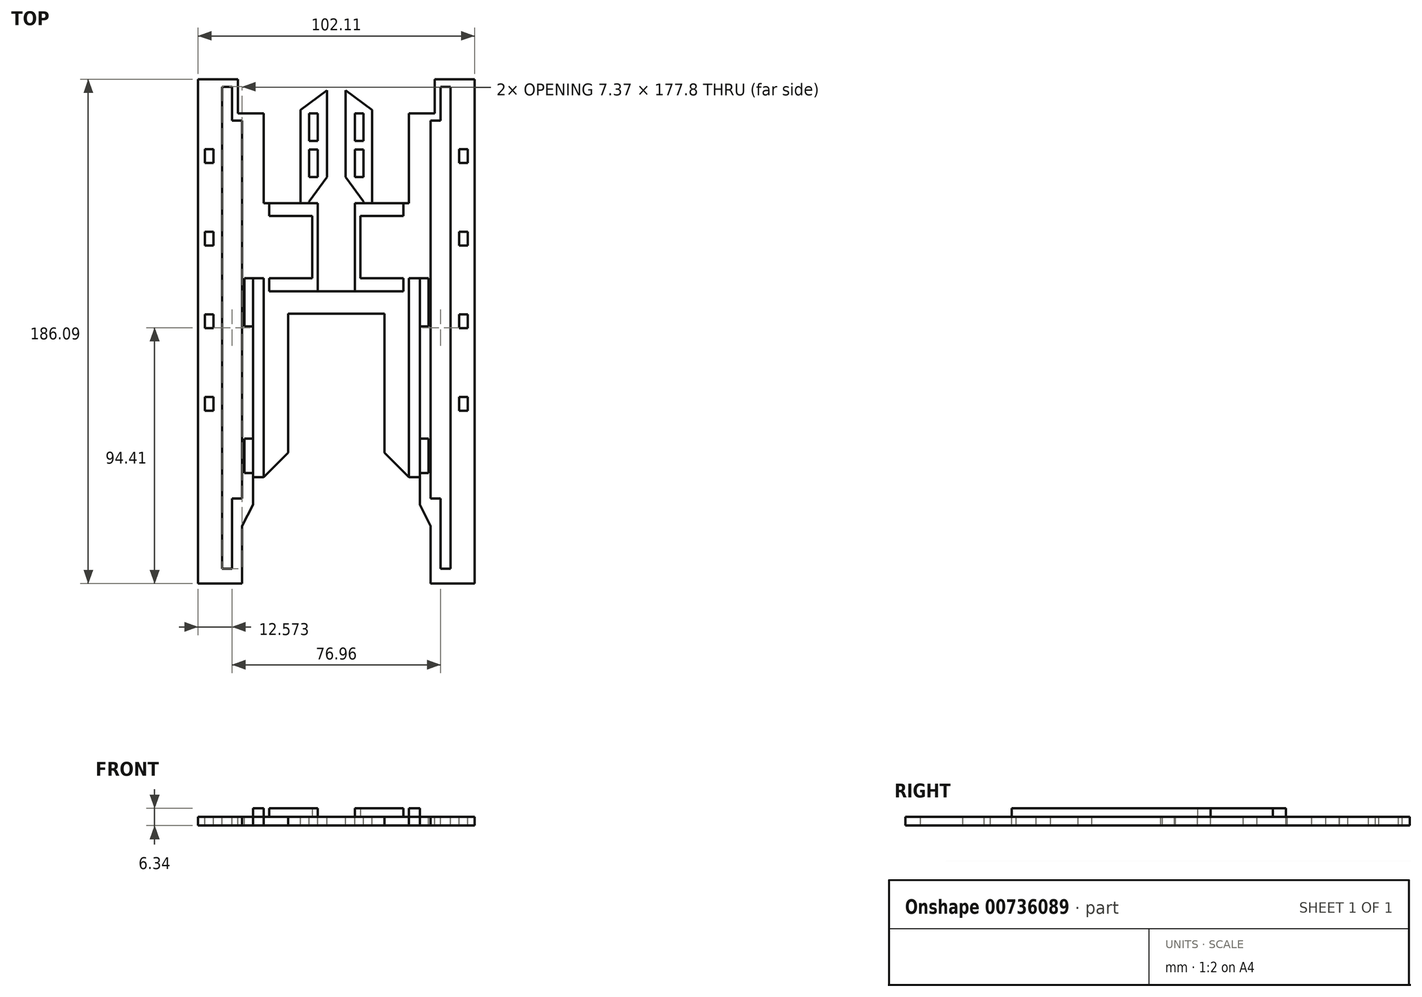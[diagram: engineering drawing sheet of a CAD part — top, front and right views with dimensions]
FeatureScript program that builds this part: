
annotation { "Feature Type Name" : "Feature", "Feature Type Description" : "" }
export const myFeature = defineFeature(function(context is Context, id is Id, definition is map)
    precondition{}
    {
        {
            var Q0;
            Q0=qCreatedBy(makeId("Top.planeOp"),FACE);
            var sketch = newSketch(context, id + "F0", { "sketchPlane" : qUnion([Q0])});
            skLineSegment(sketch, "E0.bottom", {"start": v(-53.6, 68.58) * mm, "end": v(0, 68.58) * mm});
            skLineSegment(sketch, "E0.top", {"start": v(-53.6, 0) * mm, "end": v(0, 0) * mm});
            skLineSegment(sketch, "E0.left", {"start": v(-53.6, 68.58) * mm, "end": v(-53.6, 0) * mm});
            skLineSegment(sketch, "E0.right", {"start": v(0, 68.58) * mm, "end": v(0, 0) * mm});
            skLineSegment(sketch, "E1", {"start": v(-53.6, 0) * mm, "end": v(-44.61, 8.98) * mm});
            skLineSegment(sketch, "E2", {"start": v(-44.61, 8.98) * mm, "end": v(-44.61, 68.58) * mm});
            skLineSegment(sketch, "E3", {"start": v(-53.6, 68.58) * mm, "end": v(-53.6, 73.33) * mm});
            skLineSegment(sketch, "E4", {"start": v(-53.6, 73.33) * mm, "end": v(-57.6, 73.33) * mm});
            skLineSegment(sketch, "E5", {"start": v(-57.6, 73.33) * mm, "end": v(-57.6, 0) * mm});
            skLineSegment(sketch, "E6", {"start": v(-57.6, 0) * mm, "end": v(-53.6, 0) * mm});
            skLineSegment(sketch, "E7", {"start": v(-53.6, 68.58) * mm, "end": v(-51.6, 68.58) * mm});
            skLineSegment(sketch, "E8", {"start": v(-53.6, 73.33) * mm, "end": v(-35.64, 73.33) * mm});
            skLineSegment(sketch, "E9", {"start": v(-35.64, 73.33) * mm, "end": v(-35.64, 96.37) * mm});
            skLineSegment(sketch, "E10", {"start": v(-51.6, 68.58) * mm, "end": v(-51.6, 73.33) * mm});
            skLineSegment(sketch, "E11", {"start": v(-26.8, 0) * mm, "end": v(-26.8, 68.58) * mm});
            skLineSegment(sketch, "E12", {"start": v(-33.62, 90.8) * mm, "end": v(-33.62, 68.58) * mm});
            skLineSegment(sketch, "E13", {"start": v(-35.64, 96.37) * mm, "end": v(-51.59, 96.37) * mm});
            skLineSegment(sketch, "E14", {"start": v(-53.6, 73.33) * mm, "end": v(-53.6, 96.37) * mm});
            skLineSegment(sketch, "E15", {"start": v(-53.6, 96.37) * mm, "end": v(-51.59, 96.37) * mm});
            skLineSegment(sketch, "E16", {"start": v(-53.6, 96.37) * mm, "end": v(-53.6, 101.12) * mm});
            skLineSegment(sketch, "E17", {"start": v(-53.6, 101.12) * mm, "end": v(-33.62, 101.12) * mm});
            skLineSegment(sketch, "E18", {"start": v(-33.62, 101.12) * mm, "end": v(-33.62, 90.8) * mm});
            skLineSegment(sketch, "E19", {"start": v(-51.59, 96.37) * mm, "end": v(-51.59, 101.12) * mm});
            skLineSegment(sketch, "E20", {"start": v(-57.6, 73.33) * mm, "end": v(-57.6, 55.55) * mm});
            skLineSegment(sketch, "E21", {"start": v(-57.6, 55.55) * mm, "end": v(-60.77, 55.55) * mm});
            skLineSegment(sketch, "E22", {"start": v(-60.77, 55.55) * mm, "end": v(-60.77, 73.33) * mm});
            skLineSegment(sketch, "E23", {"start": v(-60.77, 73.33) * mm, "end": v(-57.6, 73.33) * mm});
            skLineSegment(sketch, "E24", {"start": v(-60.77, 73.33) * mm, "end": v(-61.6, 73.33) * mm});
            skLineSegment(sketch, "E25", {"start": v(-57.6, 0) * mm, "end": v(-57.6, 1.54) * mm});
            skPoint(sketch, "E25.endSnap0", {"position": v(-49.1, 4.5) * mm});
            skLineSegment(sketch, "E26", {"start": v(-57.6, 1.54) * mm, "end": v(-60.77, 1.54) * mm});
            skLineSegment(sketch, "E27", {"start": v(-60.77, 1.54) * mm, "end": v(-60.77, 14.24) * mm});
            skLineSegment(sketch, "E28", {"start": v(-60.77, 14.24) * mm, "end": v(-57.6, 14.24) * mm});
            skLineSegment(sketch, "E29", {"start": v(-61.6, 73.33) * mm, "end": v(-61.6, -7.9) * mm});
            skLineSegment(sketch, "E30", {"start": v(-61.6, -7.9) * mm, "end": v(-57.6, 0) * mm});
            skLineSegment(sketch, "E31", {"start": v(-61.6, -7.9) * mm, "end": v(-65.28, -7.9) * mm});
            skLineSegment(sketch, "E32", {"start": v(-65.28, -7.9) * mm, "end": v(-65.28, -33.74) * mm});
            skLineSegment(sketch, "E33", {"start": v(-65.28, -33.74) * mm, "end": v(-68.96, -33.74) * mm});
            skLineSegment(sketch, "E34", {"start": v(-68.96, -33.74) * mm, "end": v(-68.96, 144.06) * mm});
            skLineSegment(sketch, "E35", {"start": v(-68.96, 144.06) * mm, "end": v(-65.28, 144.06) * mm});
            skLineSegment(sketch, "E36", {"start": v(-65.28, 144.06) * mm, "end": v(-65.28, 131.61) * mm});
            skLineSegment(sketch, "E37", {"start": v(-65.28, 131.61) * mm, "end": v(-61.6, 131.61) * mm});
            skLineSegment(sketch, "E38", {"start": v(-61.6, 131.61) * mm, "end": v(-61.6, 73.33) * mm});
            skLineSegment(sketch, "E39", {"start": v(-53.6, 101.12) * mm, "end": v(-53.6, 134.17) * mm});
            skLineSegment(sketch, "E40", {"start": v(-77.85, 146.84) * mm, "end": v(-77.85, -39.25) * mm});
            skLineSegment(sketch, "E41", {"start": v(-77.85, -39.25) * mm, "end": v(-61.6, -39.25) * mm});
            skLineSegment(sketch, "E42", {"start": v(-61.6, -39.25) * mm, "end": v(-61.6, -18.06) * mm});
            skLineSegment(sketch, "E43", {"start": v(-61.6, -18.06) * mm, "end": v(-57.6, -10.16) * mm});
            skLineSegment(sketch, "E44", {"start": v(-57.6, -10.16) * mm, "end": v(-57.6, 0) * mm});
            skLineSegment(sketch, "E45", {"start": v(-65.28, -33.74) * mm, "end": v(-65.28, -39.25) * mm});
            skLineSegment(sketch, "E46", {"start": v(-65.28, -39.25) * mm, "end": v(-61.6, -39.25) * mm});
            skLineSegment(sketch, "E47", {"start": v(-44.61, 60.36) * mm, "end": v(-26.8, 60.36) * mm});
            skLineSegment(sketch, "E48", {"start": v(-36.8, 134.17) * mm, "end": v(-36.8, 124) * mm});
            skLineSegment(sketch, "E49", {"start": v(-36.8, 124) * mm, "end": v(-36.8, 120.83) * mm});
            skLineSegment(sketch, "E50", {"start": v(-36.8, 120.83) * mm, "end": v(-36.8, 110.67) * mm});
            skLineSegment(sketch, "E51", {"start": v(-36.8, 110.67) * mm, "end": v(-33.62, 110.67) * mm});
            skLineSegment(sketch, "E52", {"start": v(-33.62, 110.67) * mm, "end": v(-33.62, 134.17) * mm});
            skLineSegment(sketch, "E53", {"start": v(-33.62, 134.17) * mm, "end": v(-36.8, 134.17) * mm});
            skLineSegment(sketch, "E54", {"start": v(-33.62, 110.67) * mm, "end": v(-30.2, 110.67) * mm});
            skLineSegment(sketch, "E55", {"start": v(-30.2, 110.67) * mm, "end": v(-36.8, 101.66) * mm});
            skLineSegment(sketch, "E56", {"start": v(-30.2, 110.67) * mm, "end": v(-30.2, 142.73) * mm});
            skLineSegment(sketch, "E57", {"start": v(-33.62, 101.12) * mm, "end": v(-36.8, 101.12) * mm});
            skLineSegment(sketch, "E58", {"start": v(-36.8, 110.67) * mm, "end": v(-36.8, 101.12) * mm});
            skLineSegment(sketch, "E59", {"start": v(-36.8, 101.12) * mm, "end": v(-39.97, 101.12) * mm});
            skLineSegment(sketch, "E60", {"start": v(-39.97, 101.12) * mm, "end": v(-39.97, 135.48) * mm});
            skLineSegment(sketch, "E61", {"start": v(-30.2, 142.73) * mm, "end": v(-39.97, 135.48) * mm});
            skLineSegment(sketch, "E62", {"start": v(-57.6, 0) * mm, "end": v(-68.96, 0) * mm});
            skLineSegment(sketch, "E63", {"start": v(-68.96, 0) * mm, "end": v(-68.96, 24.51) * mm});
            skLineSegment(sketch, "E64", {"start": v(-68.96, 24.51) * mm, "end": v(-72.14, 24.51) * mm});
            skLineSegment(sketch, "E65", {"start": v(-68.96, -30.23) * mm, "end": v(-77.85, -30.23) * mm});
            skLineSegment(sketch, "E66", {"start": v(-72.14, 24.51) * mm, "end": v(-75.31, 24.51) * mm});
            skLineSegment(sketch, "E67", {"start": v(-75.31, 24.51) * mm, "end": v(-75.31, 29.6) * mm});
            skLineSegment(sketch, "E68", {"start": v(-75.31, 29.6) * mm, "end": v(-72.14, 29.6) * mm});
            skLineSegment(sketch, "E69", {"start": v(-72.14, 29.6) * mm, "end": v(-72.14, 24.51) * mm});
            skLineSegment(sketch, "E70", {"start": v(-75.31, 29.6) * mm, "end": v(-75.31, 55) * mm});
            skLineSegment(sketch, "E71", {"start": v(-75.31, 55) * mm, "end": v(-72.14, 55) * mm});
            skLineSegment(sketch, "E72", {"start": v(-72.14, 55) * mm, "end": v(-72.14, 60.07) * mm});
            skLineSegment(sketch, "E73", {"start": v(-72.14, 60.07) * mm, "end": v(-75.31, 60.07) * mm});
            skLineSegment(sketch, "E74", {"start": v(-75.31, 60.07) * mm, "end": v(-75.31, 55) * mm});
            skLineSegment(sketch, "E75", {"start": v(-75.31, 60.07) * mm, "end": v(-75.31, 85.47) * mm});
            skLineSegment(sketch, "E76", {"start": v(-75.31, 85.47) * mm, "end": v(-72.14, 85.47) * mm});
            skLineSegment(sketch, "E77", {"start": v(-72.14, 85.47) * mm, "end": v(-72.14, 90.55) * mm});
            skLineSegment(sketch, "E78", {"start": v(-72.14, 90.55) * mm, "end": v(-75.31, 90.55) * mm});
            skLineSegment(sketch, "E79", {"start": v(-75.31, 90.55) * mm, "end": v(-75.31, 85.47) * mm});
            skLineSegment(sketch, "E80", {"start": v(-75.31, 90.55) * mm, "end": v(-75.31, 115.95) * mm});
            skLineSegment(sketch, "E81", {"start": v(-75.31, 115.95) * mm, "end": v(-72.14, 115.95) * mm});
            skLineSegment(sketch, "E82", {"start": v(-72.14, 115.95) * mm, "end": v(-72.14, 121.03) * mm});
            skLineSegment(sketch, "E83", {"start": v(-72.14, 121.03) * mm, "end": v(-75.31, 121.03) * mm});
            skLineSegment(sketch, "E84", {"start": v(-75.31, 121.03) * mm, "end": v(-75.31, 115.95) * mm});
            skLineSegment(sketch, "E85.MirrorCS", {"start": v(0, 68.58) * mm, "end": v(0, 73.33) * mm});
            skLineSegment(sketch, "E86.MirrorCS", {"start": v(7.17, 73.33) * mm, "end": v(4, 73.33) * mm});
            skLineSegment(sketch, "E87.MirrorCS", {"start": v(4, 0) * mm, "end": v(4, 1.54) * mm});
            skLineSegment(sketch, "E88.MirrorCS", {"start": v(-2, 68.58) * mm, "end": v(-2, 73.33) * mm});
            skLineSegment(sketch, "E89.MirrorCS", {"start": v(0, 73.33) * mm, "end": v(4, 73.33) * mm});
            skLineSegment(sketch, "E90.MirrorCS", {"start": v(0, 68.58) * mm, "end": v(-2, 68.58) * mm});
            skLineSegment(sketch, "E91.MirrorCS", {"start": v(8, -7.9) * mm, "end": v(4, 0) * mm});
            skLineSegment(sketch, "E92.MirrorCS", {"start": v(4, 1.54) * mm, "end": v(7.17, 1.54) * mm});
            skLineSegment(sketch, "E93.MirrorCS", {"start": v(4, 0) * mm, "end": v(0, 0) * mm});
            skLineSegment(sketch, "E94.MirrorCS", {"start": v(7.17, 73.33) * mm, "end": v(8, 73.33) * mm});
            skLineSegment(sketch, "E95.MirrorCS", {"start": v(0, 96.37) * mm, "end": v(-2, 96.37) * mm});
            skLineSegment(sketch, "E96.MirrorCS", {"start": v(0, 96.37) * mm, "end": v(0, 101.12) * mm});
            skLineSegment(sketch, "E97.MirrorCS", {"start": v(-2, 96.37) * mm, "end": v(-2, 101.12) * mm});
            skLineSegment(sketch, "E98.MirrorCS", {"start": v(18.54, 29.6) * mm, "end": v(18.54, 24.51) * mm});
            skLineSegment(sketch, "E99.MirrorCS", {"start": v(8, -7.9) * mm, "end": v(11.68, -7.9) * mm});
            skLineSegment(sketch, "E100.MirrorCS", {"start": v(4, 0) * mm, "end": v(15.37, 0) * mm});
            skLineSegment(sketch, "E101.MirrorCS", {"start": v(4, -10.16) * mm, "end": v(4, 0) * mm});
            skLineSegment(sketch, "E102.MirrorCS", {"start": v(21.72, 29.6) * mm, "end": v(18.54, 29.6) * mm});
            skLineSegment(sketch, "E103.MirrorCS", {"start": v(21.72, 55) * mm, "end": v(18.54, 55) * mm});
            skLineSegment(sketch, "E104.MirrorCS", {"start": v(11.68, -33.74) * mm, "end": v(15.37, -33.74) * mm});
            skLineSegment(sketch, "E105.MirrorCS", {"start": v(21.72, 60.07) * mm, "end": v(21.72, 55) * mm});
            skLineSegment(sketch, "E106.MirrorCS", {"start": v(18.54, 24.51) * mm, "end": v(21.72, 24.51) * mm});
            skLineSegment(sketch, "E107.MirrorCS", {"start": v(18.54, 60.07) * mm, "end": v(21.72, 60.07) * mm});
            skLineSegment(sketch, "E108.MirrorCS", {"start": v(15.37, 24.51) * mm, "end": v(18.54, 24.51) * mm});
            skLineSegment(sketch, "E109.MirrorCS", {"start": v(21.72, 24.51) * mm, "end": v(21.72, 29.6) * mm});
            skLineSegment(sketch, "E110.MirrorCS", {"start": v(4, 73.33) * mm, "end": v(4, 55.55) * mm});
            skLineSegment(sketch, "E111.MirrorCS", {"start": v(11.68, -39.25) * mm, "end": v(8, -39.25) * mm});
            skLineSegment(sketch, "E112.MirrorCS", {"start": v(7.17, 55.55) * mm, "end": v(7.17, 73.33) * mm});
            skLineSegment(sketch, "E113.MirrorCS", {"start": v(11.68, -33.74) * mm, "end": v(11.68, -39.25) * mm});
            skLineSegment(sketch, "E114.MirrorCS", {"start": v(4, 55.55) * mm, "end": v(7.17, 55.55) * mm});
            skLineSegment(sketch, "E115.MirrorCS", {"start": v(18.54, 55) * mm, "end": v(18.54, 60.07) * mm});
            skLineSegment(sketch, "E116.MirrorCS", {"start": v(8, -39.25) * mm, "end": v(8, -18.06) * mm});
            skLineSegment(sketch, "E117.MirrorCS", {"start": v(7.17, 1.54) * mm, "end": v(7.17, 14.24) * mm});
            skLineSegment(sketch, "E118.MirrorCS", {"start": v(7.17, 14.24) * mm, "end": v(4, 14.24) * mm});
            skLineSegment(sketch, "E119.MirrorCS", {"start": v(21.72, 85.47) * mm, "end": v(18.54, 85.47) * mm});
            skLineSegment(sketch, "E120.MirrorCS", {"start": v(18.54, 90.55) * mm, "end": v(21.72, 90.55) * mm});
            skLineSegment(sketch, "E121.MirrorCS", {"start": v(8, -18.06) * mm, "end": v(4, -10.16) * mm});
            skLineSegment(sketch, "E122.MirrorCS", {"start": v(11.68, -7.9) * mm, "end": v(11.68, -33.74) * mm});
            skLineSegment(sketch, "E123.MirrorCS", {"start": v(18.54, 85.47) * mm, "end": v(18.54, 90.55) * mm});
            skLineSegment(sketch, "E124.MirrorCS", {"start": v(21.72, 90.55) * mm, "end": v(21.72, 85.47) * mm});
            skLineSegment(sketch, "E125.MirrorCS", {"start": v(24.26, -39.25) * mm, "end": v(8, -39.25) * mm});
            skLineSegment(sketch, "E126.MirrorCS", {"start": v(-16.8, 110.67) * mm, "end": v(-16.8, 101.12) * mm});
            skLineSegment(sketch, "E127.MirrorCS", {"start": v(0, 0) * mm, "end": v(-8.98, 8.98) * mm});
            skLineSegment(sketch, "E128.MirrorCS", {"start": v(-16.8, 101.12) * mm, "end": v(-13.62, 101.12) * mm});
            skLineSegment(sketch, "E129.MirrorCS", {"start": v(0, 73.33) * mm, "end": v(0, 96.37) * mm});
            skLineSegment(sketch, "E130.MirrorCS", {"start": v(21.72, 60.07) * mm, "end": v(21.72, 85.47) * mm});
            skPoint(sketch, "E131.MirrorP", {"position": v(-4.5, 4.5) * mm});
            skLineSegment(sketch, "E132.MirrorCS", {"start": v(21.72, 29.6) * mm, "end": v(21.72, 55) * mm});
            skLineSegment(sketch, "E133.MirrorCS", {"start": v(15.37, -30.23) * mm, "end": v(24.26, -30.23) * mm});
            skLineSegment(sketch, "E134.MirrorCS", {"start": v(-16.8, 120.83) * mm, "end": v(-16.8, 110.67) * mm});
            skLineSegment(sketch, "E135.MirrorCS", {"start": v(15.37, 0) * mm, "end": v(15.37, 24.51) * mm});
            skLineSegment(sketch, "E136.MirrorCS", {"start": v(-13.62, 101.12) * mm, "end": v(-13.62, 135.48) * mm});
            skLineSegment(sketch, "E137.MirrorCS", {"start": v(21.72, 90.55) * mm, "end": v(21.72, 115.95) * mm});
            skLineSegment(sketch, "E138.MirrorCS", {"start": v(15.37, -33.74) * mm, "end": v(15.37, 144.06) * mm});
            skLineSegment(sketch, "E139.MirrorCS", {"start": v(4, 73.33) * mm, "end": v(4, 0) * mm});
            skLineSegment(sketch, "E140.MirrorCS", {"start": v(24.26, 146.84) * mm, "end": v(24.26, -39.25) * mm});
            skLineSegment(sketch, "E141.MirrorCS", {"start": v(8, 131.61) * mm, "end": v(8, 73.33) * mm});
            skLineSegment(sketch, "E142.MirrorCS", {"start": v(-16.8, 134.17) * mm, "end": v(-16.8, 124) * mm});
            skLineSegment(sketch, "E143.MirrorCS", {"start": v(0, 101.12) * mm, "end": v(0, 134.17) * mm});
            skLineSegment(sketch, "E144.MirrorCS", {"start": v(-8.98, 8.98) * mm, "end": v(-8.98, 68.58) * mm});
            skLineSegment(sketch, "E145.MirrorCS", {"start": v(-16.8, 124) * mm, "end": v(-16.8, 120.83) * mm});
            skLineSegment(sketch, "E146.MirrorCS", {"start": v(8, 73.33) * mm, "end": v(8, -7.9) * mm});
            skLineSegment(sketch, "E147.MirrorCS", {"start": v(-19.97, 101.12) * mm, "end": v(-16.8, 101.12) * mm});
            skLineSegment(sketch, "E148.MirrorCS", {"start": v(-19.97, 101.12) * mm, "end": v(-19.97, 90.8) * mm});
            skLineSegment(sketch, "E149.MirrorCS", {"start": v(-19.97, 110.67) * mm, "end": v(-23.4, 110.67) * mm});
            skLineSegment(sketch, "E150.MirrorCS", {"start": v(-17.96, 96.37) * mm, "end": v(-2, 96.37) * mm});
            skLineSegment(sketch, "E151.MirrorCS", {"start": v(-23.4, 110.67) * mm, "end": v(-16.8, 101.66) * mm});
            skLineSegment(sketch, "E152.MirrorCS", {"start": v(0, 101.12) * mm, "end": v(-19.97, 101.12) * mm});
            skLineSegment(sketch, "E153.MirrorCS", {"start": v(-19.97, 134.17) * mm, "end": v(-16.8, 134.17) * mm});
            skLineSegment(sketch, "E154.MirrorCS", {"start": v(-16.8, 110.67) * mm, "end": v(-19.97, 110.67) * mm});
            skLineSegment(sketch, "E155.MirrorCS", {"start": v(-23.4, 142.73) * mm, "end": v(-13.62, 135.48) * mm});
            skLineSegment(sketch, "E156.MirrorCS", {"start": v(-19.97, 110.67) * mm, "end": v(-19.97, 134.17) * mm});
            skLineSegment(sketch, "E157.MirrorCS", {"start": v(-17.96, 73.33) * mm, "end": v(-17.96, 96.37) * mm});
            skLineSegment(sketch, "E158.MirrorCS", {"start": v(-23.4, 110.67) * mm, "end": v(-23.4, 142.73) * mm});
            skLineSegment(sketch, "E159.MirrorCS", {"start": v(-19.97, 90.8) * mm, "end": v(-19.97, 68.58) * mm});
            skLineSegment(sketch, "E160.MirrorCS", {"start": v(0, 73.33) * mm, "end": v(-17.96, 73.33) * mm});
            skLineSegment(sketch, "E161.MirrorCS", {"start": v(0, 68.58) * mm, "end": v(-53.6, 68.58) * mm});
            skLineSegment(sketch, "E162.MirrorCS", {"start": v(0, 0) * mm, "end": v(-53.6, 0) * mm});
            skLineSegment(sketch, "E163.MirrorCS", {"start": v(-8.98, 60.36) * mm, "end": v(-26.8, 60.36) * mm});
            skLineSegment(sketch, "E164", {"start": v(-36.8, 124) * mm, "end": v(-33.62, 124) * mm});
            skLineSegment(sketch, "E165", {"start": v(-36.8, 120.83) * mm, "end": v(-33.62, 120.83) * mm});
            skLineSegment(sketch, "E166", {"start": v(-53.6, 134.17) * mm, "end": v(-63.13, 134.17) * mm});
            skLineSegment(sketch, "E167", {"start": v(-63.13, 134.17) * mm, "end": v(-63.13, 146.84) * mm});
            skLineSegment(sketch, "E168", {"start": v(-77.85, 146.84) * mm, "end": v(-63.13, 146.84) * mm});
            skLineSegment(sketch, "E169.MirrorCS", {"start": v(9.53, 134.17) * mm, "end": v(9.53, 146.84) * mm});
            skLineSegment(sketch, "E170.MirrorCS", {"start": v(11.68, 131.61) * mm, "end": v(8, 131.61) * mm});
            skLineSegment(sketch, "E171.MirrorCS", {"start": v(18.54, 115.95) * mm, "end": v(18.54, 121.03) * mm});
            skLineSegment(sketch, "E172.MirrorCS", {"start": v(21.72, 115.95) * mm, "end": v(18.54, 115.95) * mm});
            skLineSegment(sketch, "E173.MirrorCS", {"start": v(21.72, 121.03) * mm, "end": v(21.72, 115.95) * mm});
            skLineSegment(sketch, "E174.MirrorCS", {"start": v(24.26, 146.84) * mm, "end": v(9.53, 146.84) * mm});
            skLineSegment(sketch, "E175.MirrorCS", {"start": v(18.54, 121.03) * mm, "end": v(21.72, 121.03) * mm});
            skLineSegment(sketch, "E176.MirrorCS", {"start": v(11.68, 144.06) * mm, "end": v(11.68, 131.61) * mm});
            skLineSegment(sketch, "E177.MirrorCS", {"start": v(15.37, 144.06) * mm, "end": v(11.68, 144.06) * mm});
            skLineSegment(sketch, "E178.MirrorCS", {"start": v(0, 134.17) * mm, "end": v(9.53, 134.17) * mm});
            skLineSegment(sketch, "E179.MirrorCS", {"start": v(-16.8, 124) * mm, "end": v(-19.97, 124) * mm});
            skLineSegment(sketch, "E180.MirrorCS", {"start": v(-16.8, 120.83) * mm, "end": v(-19.97, 120.83) * mm});
            skSolve(sketch);
        }
        {
            var Q0;
            Q0=makeQuery(id+"F0.imprint","IMPRINT",FACE,{"disambiguationData":[TD([[makeQuery(id+"F0.imprint","IMPRINT",EDGE,{"derivedFrom":sQuery(id+"F0.wireOp",EDGE,"E4")}),-1.0]])]});
            var Q1;
            Q1=makeQuery(id+"F0.imprint","IMPRINT",FACE,{"disambiguationData":[TD([[makeQuery(id+"F0.imprint","IMPRINT",EDGE,{"derivedFrom":sQuery(id+"F0.wireOp",EDGE,"E0.left")}),-1.0]])]});
            var Q2;
            {var subQ1=sQuery(id+"F0.wireOp",EDGE,"E21");Q2=makeQuery(id+"F0.imprint","IMPRINT",FACE,{"disambiguationData":[TD([[makeQuery(id+"F0.imprint","IMPRINT",EDGE,{"derivedFrom":subQ1}),1.0]])]});}
            var Q3;
            Q3=makeQuery(id+"F0.imprint","IMPRINT",FACE,{"disambiguationData":[TD([[makeQuery(id+"F0.imprint","IMPRINT",EDGE,{"derivedFrom":sQuery(id+"F0.wireOp",EDGE,"E30")}),-1.0]])]});
            var Q4;
            {var subQ0=sQuery(id+"F0.wireOp",EDGE,"E30");Q4=makeQuery(id+"F0.imprint","IMPRINT",FACE,{"disambiguationData":[TD([[makeQuery(id+"F0.imprint","IMPRINT",EDGE,{"derivedFrom":subQ0}),1.0]])]});}
            var Q5;
            {var subQ1=sQuery(id+"F0.wireOp",EDGE,"E33");Q5=makeQuery(id+"F0.imprint","IMPRINT",FACE,{"disambiguationData":[TD([[makeQuery(id+"F0.imprint","IMPRINT",EDGE,{"derivedFrom":subQ1}),1.0]])]});}
            var Q6;
            {var subQ5=sQuery(id+"F0.wireOp",EDGE,"E0.left");Q6=makeQuery(id+"F0.imprint","IMPRINT",FACE,{"disambiguationData":[TD([[makeQuery(id+"F0.imprint","IMPRINT",EDGE,{"derivedFrom":subQ5}),1.0]])]});}
            var Q7;
            {var subQ4=sQuery(id+"F0.wireOp",EDGE,"E47");Q7=makeQuery(id+"F0.imprint","IMPRINT",FACE,{"disambiguationData":[TD([[makeQuery(id+"F0.imprint","IMPRINT",EDGE,{"derivedFrom":subQ4}),1.0]])]});}
            var Q8;
            {var subQ3=sQuery(id+"F0.wireOp",EDGE,"E9");Q8=makeQuery(id+"F0.imprint","IMPRINT",FACE,{"disambiguationData":[TD([[makeQuery(id+"F0.imprint","IMPRINT",EDGE,{"derivedFrom":subQ3}),-1.0]])]});}
            var Q9;
            {var subQ0=sQuery(id+"F0.wireOp",EDGE,"E9");Q9=makeQuery(id+"F0.imprint","IMPRINT",FACE,{"disambiguationData":[TD([[makeQuery(id+"F0.imprint","IMPRINT",EDGE,{"derivedFrom":subQ0}),1.0]])]});}
            var Q10;
            Q10=makeQuery(id+"F0.imprint","IMPRINT",FACE,{"disambiguationData":[TD([[makeQuery(id+"F0.imprint","IMPRINT",EDGE,{"derivedFrom":sQuery(id+"F0.wireOp",EDGE,"E15")}),1.0]])]});
            var Q11;
            {var subQ0=sQuery(id+"F0.wireOp",EDGE,"E3");Q11=makeQuery(id+"F0.imprint","IMPRINT",FACE,{"disambiguationData":[TD([[makeQuery(id+"F0.imprint","IMPRINT",EDGE,{"derivedFrom":subQ0}),-1.0]])]});}
            var Q12;
            {var subQ0=sQuery(id+"F0.wireOp",EDGE,"E163.MirrorCS");Q12=makeQuery(id+"F0.imprint","IMPRINT",FACE,{"disambiguationData":[TD([[makeQuery(id+"F0.imprint","IMPRINT",EDGE,{"derivedFrom":subQ0}),-1.0]])]});}
            var Q13;
            Q13=makeQuery(id+"F0.imprint","IMPRINT",FACE,{"disambiguationData":[TD([[makeQuery(id+"F0.imprint","IMPRINT",EDGE,{"derivedFrom":sQuery(id+"F0.wireOp",EDGE,"E0.right")}),-1.0]])]});
            var Q14;
            {var subQ4=sQuery(id+"F0.wireOp",EDGE,"E88.MirrorCS");Q14=makeQuery(id+"F0.imprint","IMPRINT",FACE,{"disambiguationData":[TD([[makeQuery(id+"F0.imprint","IMPRINT",EDGE,{"derivedFrom":subQ4}),1.0]])]});}
            var Q15;
            Q15=makeQuery(id+"F0.imprint","IMPRINT",FACE,{"disambiguationData":[TD([[makeQuery(id+"F0.imprint","IMPRINT",EDGE,{"derivedFrom":sQuery(id+"F0.wireOp",EDGE,"E95.MirrorCS")}),1.0]])]});
            var Q16;
            Q16=makeQuery(id+"F0.imprint","IMPRINT",FACE,{"disambiguationData":[TD([[makeQuery(id+"F0.imprint","IMPRINT",EDGE,{"derivedFrom":sQuery(id+"F0.wireOp",EDGE,"E95.MirrorCS")}),-1.0]])]});
            var Q17;
            {var subQ0=sQuery(id+"F0.wireOp",EDGE,"E85.MirrorCS");Q17=makeQuery(id+"F0.imprint","IMPRINT",FACE,{"disambiguationData":[TD([[makeQuery(id+"F0.imprint","IMPRINT",EDGE,{"derivedFrom":subQ0}),1.0]])]});}
            var Q18;
            {var subQ4=sQuery(id+"F0.wireOp",EDGE,"E93.MirrorCS");Q18=makeQuery(id+"F0.imprint","IMPRINT",FACE,{"disambiguationData":[TD([[makeQuery(id+"F0.imprint","IMPRINT",EDGE,{"derivedFrom":subQ4}),-1.0]])]});}
            var Q19;
            Q19=makeQuery(id+"F0.imprint","IMPRINT",FACE,{"disambiguationData":[TD([[makeQuery(id+"F0.imprint","IMPRINT",EDGE,{"derivedFrom":sQuery(id+"F0.wireOp",EDGE,"E109.MirrorCS")}),-1.0]])]});
            var Q20;
            {var subQ7=sQuery(id+"F0.wireOp",EDGE,"E118.MirrorCS");Q20=makeQuery(id+"F0.imprint","IMPRINT",FACE,{"disambiguationData":[TD([[makeQuery(id+"F0.imprint","IMPRINT",EDGE,{"derivedFrom":subQ7}),-1.0]])]});}
            var Q21;
            {var subQ3=sQuery(id+"F0.wireOp",EDGE,"E113.MirrorCS");Q21=makeQuery(id+"F0.imprint","IMPRINT",FACE,{"disambiguationData":[TD([[makeQuery(id+"F0.imprint","IMPRINT",EDGE,{"derivedFrom":subQ3}),1.0]])]});}
            var Q22;
            Q22=makeQuery(id+"F0.imprint","IMPRINT",FACE,{"disambiguationData":[TD([[makeQuery(id+"F0.imprint","IMPRINT",EDGE,{"derivedFrom":sQuery(id+"F0.wireOp",EDGE,"E91.MirrorCS")}),1.0]])]});
            var Q23;
            {var subQ0=sQuery(id+"F0.wireOp",EDGE,"E91.MirrorCS");Q23=makeQuery(id+"F0.imprint","IMPRINT",FACE,{"disambiguationData":[TD([[makeQuery(id+"F0.imprint","IMPRINT",EDGE,{"derivedFrom":subQ0}),-1.0]])]});}
            var Q24;
            {var subQ0=sQuery(id+"F0.wireOp",EDGE,"E51");Q24=makeQuery(id+"F0.imprint","IMPRINT",FACE,{"disambiguationData":[TD([[makeQuery(id+"F0.imprint","IMPRINT",EDGE,{"derivedFrom":subQ0}),-1.0]])]});}
            var Q25;
            Q25=makeQuery(id+"F0.imprint","IMPRINT",FACE,{"disambiguationData":[TD([[makeQuery(id+"F0.imprint","IMPRINT",EDGE,{"derivedFrom":sQuery(id+"F0.wireOp",EDGE,"E48")}),-1.0]])]});
            var Q26;
            Q26=makeQuery(id+"F0.imprint","IMPRINT",FACE,{"disambiguationData":[TD([[makeQuery(id+"F0.imprint","IMPRINT",EDGE,{"derivedFrom":sQuery(id+"F0.wireOp",EDGE,"E49")}),1.0]])]});
            var Q27;
            {var subQ0=sQuery(id+"F0.wireOp",EDGE,"E179.MirrorCS");Q27=makeQuery(id+"F0.imprint","IMPRINT",FACE,{"disambiguationData":[TD([[makeQuery(id+"F0.imprint","IMPRINT",EDGE,{"derivedFrom":subQ0}),1.0]])]});}
            var Q28;
            {var subQ7=sQuery(id+"F0.wireOp",EDGE,"E149.MirrorCS");Q28=makeQuery(id+"F0.imprint","IMPRINT",FACE,{"disambiguationData":[TD([[makeQuery(id+"F0.imprint","IMPRINT",EDGE,{"derivedFrom":subQ7}),-1.0]])]});}
            var Q29;
            Q29=makeQuery(id+"F0.imprint","IMPRINT",FACE,{"disambiguationData":[TD([[makeQuery(id+"F0.imprint","IMPRINT",EDGE,{"derivedFrom":sQuery(id+"F0.wireOp",EDGE,"E149.MirrorCS")}),1.0]])]});
            extrude(context, id + "F1", {"entities" : qUnion([Q0, Q1, Q2, Q3, Q4, Q5, Q6, Q7, Q8, Q9, Q10, Q11, Q12, Q13, Q14, Q15, Q16, Q17, Q18, Q19, Q20, Q21, Q22, Q23, Q24, Q25, Q26, Q27, Q28, Q29]), "oppositeDirection" : true, "depth" : 3.17 * mm, "offsetDistance" : 25.4 * mm});
        }
        {
            var Q0;
            {var subQ4=sQuery(id+"F0.wireOp",EDGE,"E93.MirrorCS");Q0=makeQuery(id+"F0.imprint","IMPRINT",FACE,{"disambiguationData":[TD([[makeQuery(id+"F0.imprint","IMPRINT",EDGE,{"derivedFrom":subQ4}),-1.0]])]});}
            var Q1;
            {var subQ4=sQuery(id+"F0.wireOp",EDGE,"E88.MirrorCS");Q1=makeQuery(id+"F0.imprint","IMPRINT",FACE,{"disambiguationData":[TD([[makeQuery(id+"F0.imprint","IMPRINT",EDGE,{"derivedFrom":subQ4}),1.0]])]});}
            var Q2;
            {var subQ3=sQuery(id+"F0.wireOp",EDGE,"E9");Q2=makeQuery(id+"F0.imprint","IMPRINT",FACE,{"disambiguationData":[TD([[makeQuery(id+"F0.imprint","IMPRINT",EDGE,{"derivedFrom":subQ3}),-1.0]])]});}
            var Q3;
            Q3=makeQuery(id+"F0.imprint","IMPRINT",FACE,{"disambiguationData":[TD([[makeQuery(id+"F0.imprint","IMPRINT",EDGE,{"derivedFrom":sQuery(id+"F0.wireOp",EDGE,"E0.left")}),-1.0]])]});
            extrude(context, id + "F2", {"entities" : qUnion([Q0, Q1, Q2, Q3]), "depth" : 3.17 * mm, "offsetDistance" : 25.4 * mm});
        }
    });
